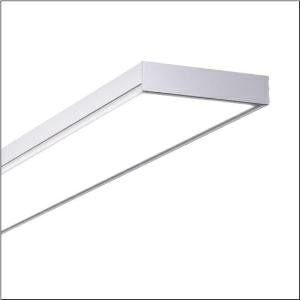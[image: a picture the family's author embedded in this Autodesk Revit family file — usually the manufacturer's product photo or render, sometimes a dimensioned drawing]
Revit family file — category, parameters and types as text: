
# Revit family: apollon_r__31_surface_51mp26wd2441e_9924
name_source: partatom
category: Lighting Fixtures
units: mm (PartAtom-declared; Revit-internal decimal feet)

## family parameters
Cut with Voids When Loaded = No
Host = Face
Light Source = No
Part Type = Normal
Room Calculation Point = No
Round Connector Dimension = Use Diameter
Shared = No

## types (1)
- Apollon® 31 Surface (1 x LED, 4600 lm, 33 W, 4000K)
    Apparent Load = 33 VA
    CIE Flux Codes = 61 87 97 97 100
    Color Rendering = 80
    Color Temperature = 4000K
    Default Elevation = 1800 mm
    Description = Apollon® 31 Surface, office luminaire, primary optical cover: micro prismatic cover, of PMMA, light emission: direct distribution, primary light characteristic: symmetric, installation type: surface-mounted, LED, rated luminous flux: 4.600lm, luminous efficacy: 139lm/W, light colour: 840, colour temperature: 4000K, control gear: ECG DALI, with terminal, 5-pole, mains connection: 220..240V, AC, 50/60Hz, rated input power: 33W, housing, of sheet steel, coil coated, metallic grey (RAL 9006), length: 1.545mm, width: 200mm, height: 44mm, protection rating (complete): IP20, insulation class (complete): insulation class II (safety insulation), certification: CE, impact resistance: IK02, permissible operating ambient temperature: -20..+40°C, standard: EN 60598-2-22, packaging unit: 1 piece
    Height = 44 mm
    Lamp = 1 x LED
    Lamp Light Flux = 4600 lm
    Lamp Power = 33 W
    Lamp count = 1
    Length = 1545 mm
    Luminous efficacy = 139 lm/W
    Manufacturer = Siteco
    ModVariant = No
    Model = 51MP26WD2441E
    Mounting Place = Ceiling
    Mounting Type = Surface mounted
    Number of Poles = 1
    OnlyDefault = Yes
    Power Factor = 1
    Product Name = Apollon® 31 Surface
    Product group = office luminaire | ceiling mounted
    ProductGroupID = 300
    Protection Class = Protection class II
    Protection Degree = IP 20
    RLX_Detail_Level = 1
    RLX_Emergency_Light_Flux = 0 lm
    RLX_Emergency_Type = 0
    RLX_Emergency_Type_DB = No
    RlxData = <blob elided: 24117 chars, md5=178626d8>
    Socket = socket
    Standby Power = 0 W
    System Light Flux = 4600 lm
    System Power = 33 W
    Type Comments = Product without accessories
    Type Image = l_1313654.jpg
    URL = http://relux.com
    VarID = ---
    Voltage = 0 V
    Weight = 0.00 kg
    Width = 200 mm  [stored 0.656168 ft]

note: [stored X ft] marks values corroborated as IEEE doubles in the binary element streams (Revit-internal decimal feet)

## geometry (parser evidence)
native form markers: Blend x4, Sweep x10
no freeform markers — native parametric forms only
